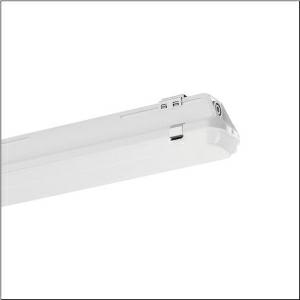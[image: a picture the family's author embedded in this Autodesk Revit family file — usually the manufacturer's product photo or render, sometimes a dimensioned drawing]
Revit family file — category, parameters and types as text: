
# Revit family: monsun_11_51fp10ep460l
name_source: partatom
category: Lighting Fixtures
units: mm (PartAtom-declared; Revit-internal decimal feet)

## family parameters
Cut with Voids When Loaded = No
Host = Face
Light Source = No
Part Type = Normal
Room Calculation Point = No
Round Connector Dimension = Use Diameter
Shared = No

## types (1)
- --- (1 x LED, 6050 lm, 31.5 W, 4000K)
    Apparent Load = 32 VA
    CIE Flux Codes = 47 77 93 94 100
    Color Rendering = 80
    Color Temperature = 4000K
    Default Elevation = 1800 mm
    Description = Monsun 11, damp-proof luminaire, chain hanger, primary optical cover: enclosure, of PMMA, light emission: direct distribution, primary light characteristic: symmetric, installation type: suspended mounting, surface-mounted, horizontal mounting, vertical mounting, LED, rated luminous flux: 6.050lm, luminous efficacy: 192lm/W, light colour: 840, colour temperature: 4000K, control gear: DALI 2, with terminal, 5-pole, max. 2.5mm², mains connection: 220..240V, AC, 50/60Hz, rated input power: 32W, luminaire housing, of glass-fibre reinforced polyester, uncoated, bright grey, incl. chain hanger, length: 1.590mm, width: 90mm, height: 88mm, clip for enclosure, of stainless steel (V2A), ceiling mounting element, of stainless steel (V2A), chain hanger, of stainless steel (V2A), protection rating (complete): IP66, insulation class (complete): insulation class I (protective earthing), certification: CE, ENEC, VDE, UKCA, protection symbol: D, impact resistance: IK04, permissible operating ambient temperature: -25..+35°C, standard: EN 50419, EN 60598-2-1, corresponds to IFS (International Featured Standards) requirements for safety and quality in the food industry, for indoor or canopied outdoor use, no direct snow, no direct sun, no direct rain, LABS conformity tested according to VDMA 24364:2018-05, contact your sales advisor before using the luminaires in applications with unclear chemical exposure, large temperature fluctuations or condensation-forming humidity, packaging unit: 1 piece
    Height = 89 mm
    Lamp = 1 x LED
    Lamp Light Flux = 6050 lm
    Lamp Power = 31.5 W
    Lamp count = 1
    Length = 1590 mm
    Luminous efficacy = 192 lm/W
    Manufacturer = Siteco
    ModVariant = No
    Model = 51FP10EP460L
    Mounting Place = Ceiling
    Mounting Type = Surface mounted
    Number of Poles = 1
    OnlyDefault = Yes
    Power Factor = 1
    Product Name = Monsun 11
    Product group = damp-proof luminaire
    ProductGroupID = 300
    Protection Class = Protection class I
    Protection Degree = IP 66
    RLX_Detail_Level = 1
    RLX_Emergency_Light_Flux = 0 lm
    RLX_Emergency_Type = 0
    RLX_Emergency_Type_DB = No
    RlxData = <blob elided: 92869 chars, md5=b36feb90>
    Socket = socket
    Standby Power = 0 W
    System Light Flux = 6050 lm
    System Power = 32 W
    Type Comments = factory setting: luminous flux: 100 % | dim-lin: 254 | 219 mA
    Type Image = l_1349237.jpg
    URL = http://relux.com
    VarID = @adj_033727
    Voltage = 0 V
    Weight = 0.00 kg
    Width = 90 mm

## geometry (parser evidence)
native form markers: Blend x4, Sweep x13
no freeform markers — native parametric forms only
